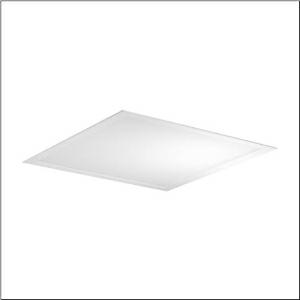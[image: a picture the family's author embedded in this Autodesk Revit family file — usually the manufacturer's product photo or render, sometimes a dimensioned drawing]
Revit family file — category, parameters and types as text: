
# Revit family: apollon_r__21_square_51mq11wd3413_f273
name_source: partatom
category: Lighting Fixtures
units: mm (PartAtom-declared; Revit-internal decimal feet)

## family parameters
Cut with Voids When Loaded = No
Host = Face
Light Source = No
Part Type = Normal
Room Calculation Point = No
Round Connector Dimension = Use Diameter
Shared = No

## types (1)
- Apollon® 21 square (1 x LED, 4200 lm, 33 W, 4000K)
    Apparent Load = 33 VA
    CIE Flux Codes = 61 87 97 100 100
    Color Rendering = 80
    Color Temperature = 4000K
    Default Elevation = 1800 mm
    Description = Apollon® 21 square, office luminaire, primary optical cover: micro prismatic cover, of PMMA, CAT 2 (L<= 3000cd/m²), light emission: direct distribution, primary light characteristic: symmetric, installation type: lay-in mounting, LED, rated luminous flux: 4.200lm, luminous efficacy: 127lm/W, light colour: 840, colour temperature: 4000K, control gear: ECG DALI, with Linect®, mains connection: 220..240V, AC, 50/60Hz, rated input power: 32W, housing, of aluminium, traffic white (RAL 9016), module: M625, length: 620mm, width: 620mm, height: 40mm, housing upper side, of sheet steel, galvanised, protection rating (complete): IP20, protection rating (lamp compartment, on room side): IP50, insulation class (complete): insulation class II (safety insulation), certification: CE, ENEC, permissible operating ambient temperature: -20..+40°C, packaging unit: 1 piece
    Height = 0 mm  [stored 0 ft]
    Lamp = 1 x LED
    Lamp Light Flux = 4200 lm
    Lamp Power = 33 W
    Lamp count = 1
    Length = 620 mm
    Luminous efficacy = 127 lm/W
    Manufacturer = Siteco
    ModVariant = No
    Model = 51MQ11WD3413
    Mounting Place = Ceiling
    Mounting Type = Recessed
    Number of Poles = 1
    OnlyDefault = Yes
    Power Factor = 1
    Product Name = Apollon® 21 square
    Product group = office luminaire | ceiling recessed
    ProductGroupID = 400
    Protection Class = Protection class II
    Protection Degree = IP 20
    RLX_Detail_Level = 1
    RlxData = <blob elided: 14897 chars, md5=a6451ea4>
    Socket = socket
    Standby Power = 0 W
    System Light Flux = 4200 lm
    System Power = 33 W
    Type Comments = Product without accessories
    Type Image = l_1006122.jpg
    URL = http://relux.com
    VarID = ---
    Voltage = 0 V
    Weight = 0.00 kg
    Width = 620 mm

note: [stored X ft] marks values corroborated as IEEE doubles in the binary element streams (Revit-internal decimal feet)

## geometry (parser evidence)
native form markers: Sweep x11
no freeform markers — native parametric forms only
